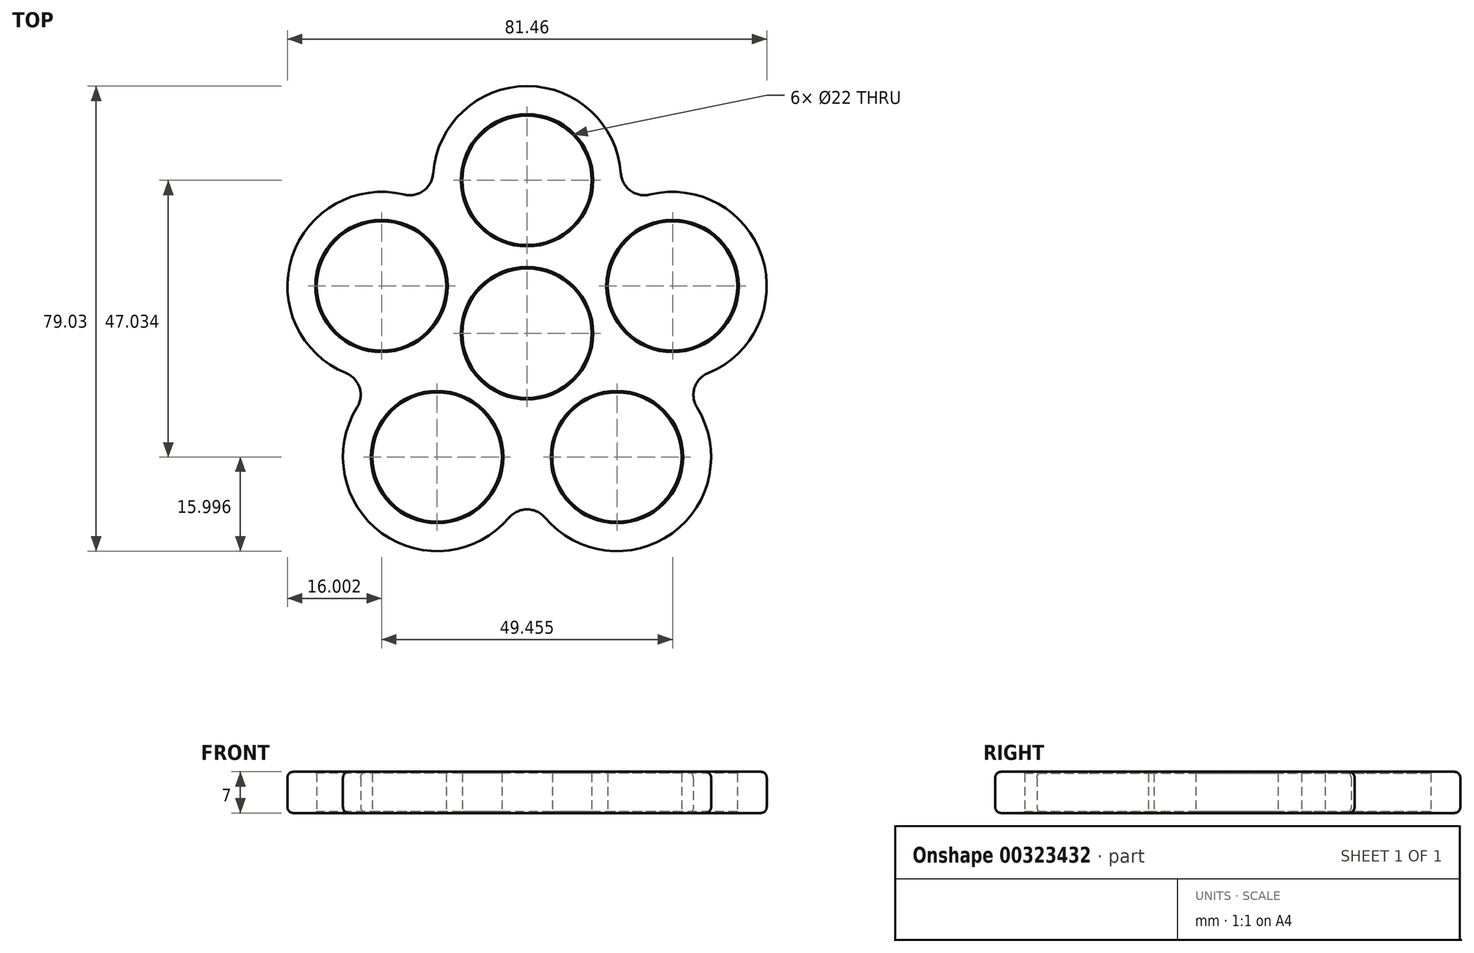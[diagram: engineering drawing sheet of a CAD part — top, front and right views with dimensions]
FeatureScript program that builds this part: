
annotation { "Feature Type Name" : "Feature", "Feature Type Description" : "" }
export const myFeature = defineFeature(function(context is Context, id is Id, definition is map)
    precondition{}
    {
        {
            var Q0;
            Q0=qCreatedBy(makeId("Top.planeOp"),FACE);
            var sketch = newSketch(context, id + "F0", { "sketchPlane" : qUnion([Q0])});
            skCircle(sketch, "E0", {"center": v(0, 0) * mm, "radius": 11 * mm});
            skLineSegment(sketch, "E1", {"start": v(0, 0) * mm, "end": v(0, 26) * mm, "construction": true});
            skLineSegment(sketch, "E2", {"start": v(0, 0) * mm, "end": v(24.73, 8.03) * mm, "construction": true});
            skLineSegment(sketch, "E3", {"start": v(0, 0) * mm, "end": v(15.28, -21.03) * mm, "construction": true});
            skLineSegment(sketch, "E4", {"start": v(0, 0) * mm, "end": v(-24.73, 8.03) * mm, "construction": true});
            skLineSegment(sketch, "E5", {"start": v(0, 0) * mm, "end": v(-15.28, -21.03) * mm, "construction": true});
            skCircle(sketch, "E6", {"center": v(0, 26) * mm, "radius": 11 * mm});
            skCircle(sketch, "E7", {"center": v(-24.73, 8.03) * mm, "radius": 11 * mm});
            skCircle(sketch, "E8", {"center": v(-15.28, -21.03) * mm, "radius": 11 * mm});
            skCircle(sketch, "E9", {"center": v(15.28, -21.03) * mm, "radius": 11 * mm});
            skCircle(sketch, "E10", {"center": v(24.73, 8.03) * mm, "radius": 11 * mm});
            skArc(sketch, "E11", {"start": v(15.96, 27.16) * mm, "mid": v(0, 42) * mm, "end": v(-15.96, 27.16) * mm});
            skArc(sketch, "E12", {"start": v(-20.9, 23.57) * mm, "mid": v(-39.94, 12.98) * mm, "end": v(-30.77, -6.78) * mm});
            skArc(sketch, "E13", {"start": v(-28.88, -12.6) * mm, "mid": v(-24.69, -33.98) * mm, "end": v(-3.06, -31.36) * mm});
            skArc(sketch, "E14", {"start": v(3.06, -31.36) * mm, "mid": v(24.69, -33.98) * mm, "end": v(28.88, -12.6) * mm});
            skArc(sketch, "E15", {"start": v(30.77, -6.78) * mm, "mid": v(39.94, 12.98) * mm, "end": v(20.9, 23.57) * mm});
            skArc(sketch, "E16", {"start": v(-20.9, 23.57) * mm, "mid": v(-17.6, 24.22) * mm, "end": v(-15.96, 27.16) * mm});
            skArc(sketch, "E17", {"start": v(-28.88, -12.6) * mm, "mid": v(-28.47, -9.25) * mm, "end": v(-30.77, -6.78) * mm});
            skArc(sketch, "E18", {"start": v(3.06, -31.36) * mm, "mid": v(0, -29.94) * mm, "end": v(-3.06, -31.36) * mm});
            skArc(sketch, "E19", {"start": v(15.96, 27.16) * mm, "mid": v(17.6, 24.22) * mm, "end": v(20.9, 23.57) * mm});
            skArc(sketch, "E20", {"start": v(30.77, -6.78) * mm, "mid": v(28.47, -9.25) * mm, "end": v(28.88, -12.6) * mm});
            skArc(sketch, "E21", {"start": v(-15.96, 27.16) * mm, "mid": v(0, 10) * mm, "end": v(15.96, 27.16) * mm, "construction": true});
            skLineSegment(sketch, "E22", {"start": v(-17.64, 15) * mm, "end": v(14.72, 15) * mm});
            skLineSegment(sketch, "E23", {"start": v(-14.74, 11) * mm, "end": v(16.44, 11) * mm});
            skSolve(sketch);
        }
        {
            var Q0;
            Q0=makeQuery(id+"F0.imprint","IMPRINT",FACE,{"disambiguationData":[TD([[makeQuery(id+"F0.imprint","IMPRINT",EDGE,{"derivedFrom":sQuery(id+"F0.wireOp",EDGE,"E0")}),-1.0]])]});
            extrude(context, id + "F1", {"entities" : qUnion([Q0]), "depth" : 7 * mm});
        }
        {
            var Q0;
            Q0=makeQuery(id+"F1.opExtrude","SWEPT_FACE",FACE,{"disambiguationData":[OSD([sQuery(id+"F0.wireOp",EDGE,"E6")])]});
            var Q1;
            Q1=makeQuery(id+"F1.opExtrude","SWEPT_FACE",FACE,{"disambiguationData":[OSD([sQuery(id+"F0.wireOp",EDGE,"E10")])]});
            var Q2;
            Q2=makeQuery(id+"F1.opExtrude","SWEPT_FACE",FACE,{"disambiguationData":[OSD([sQuery(id+"F0.wireOp",EDGE,"E0")])]});
            var Q3;
            Q3=makeQuery(id+"F1.opExtrude","SWEPT_FACE",FACE,{"disambiguationData":[OSD([sQuery(id+"F0.wireOp",EDGE,"E7")])]});
            var Q4;
            Q4=makeQuery(id+"F1.opExtrude","SWEPT_FACE",FACE,{"disambiguationData":[OSD([sQuery(id+"F0.wireOp",EDGE,"E8")])]});
            var Q5;
            Q5=makeQuery(id+"F1.opExtrude","SWEPT_FACE",FACE,{"disambiguationData":[OSD([sQuery(id+"F0.wireOp",EDGE,"E9")])]});
            chamfer(context, id + "F2", {"entities" : qUnion([Q0, Q1, Q2, Q3, Q4, Q5]), "width" : .25 * mm, "tangentPropagation" : true});
        }
        {
            var Q0;
            Q0=makeQuery(id+"F1.opExtrude","CAP_EDGE",EDGE,{"disambiguationData":[OSD([sQuery(id+"F0.wireOp",EDGE,"E18")])],"isStart":false});
            var Q1;
            Q1=makeQuery(id+"F1.opExtrude","CAP_EDGE",EDGE,{"disambiguationData":[OSD([sQuery(id+"F0.wireOp",EDGE,"E18")])],"isStart":true});
            fillet(context, id + "F3", {"entities" : qUnion([Q0, Q1]), "radius" : 1 * mm, "tangentPropagation" : true, "allowEdgeOverflow" : false});
        }
    });
